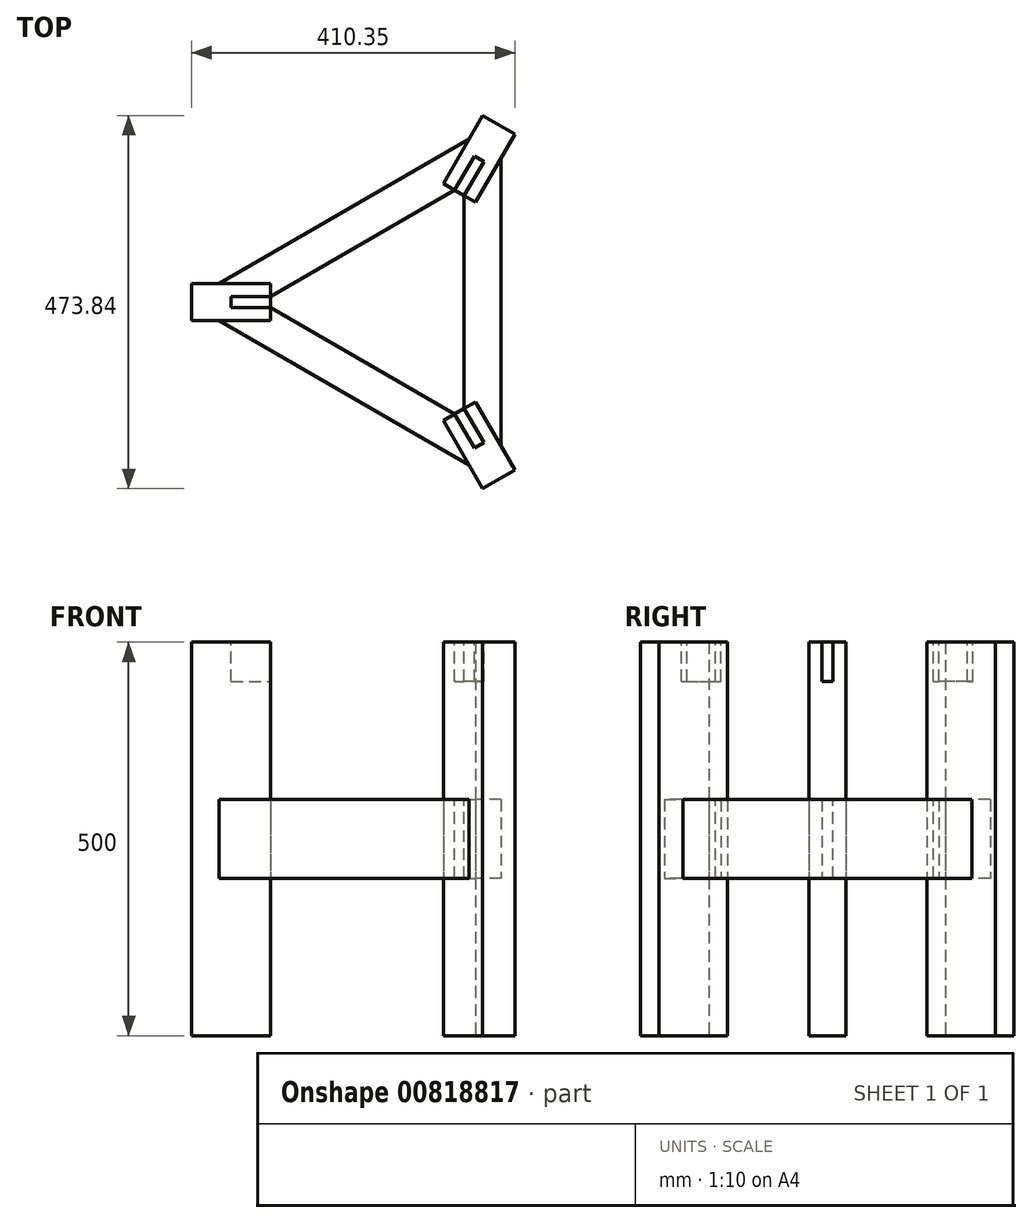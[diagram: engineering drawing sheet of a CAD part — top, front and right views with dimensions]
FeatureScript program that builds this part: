
annotation { "Feature Type Name" : "Feature", "Feature Type Description" : "" }
export const myFeature = defineFeature(function(context is Context, id is Id, definition is map)
    precondition{}
    {
        {
            var Q0;
            Q0=qCreatedBy(makeId("Top.planeOp"),FACE);
            var sketch = newSketch(context, id + "F0", { "sketchPlane" : qUnion([Q0])});
            skLineSegment(sketch, "E0.bottom", {"start": v(-160, 23.5) * mm, "end": v(-260, 23.5) * mm});
            skLineSegment(sketch, "E0.top", {"start": v(-160, -23.5) * mm, "end": v(-260, -23.5) * mm});
            skLineSegment(sketch, "E0.left", {"start": v(-160, 23.5) * mm, "end": v(-160, -23.5) * mm});
            skLineSegment(sketch, "E0.right", {"start": v(-260, 23.5) * mm, "end": v(-260, -23.5) * mm});
            skPoint(sketch, "E0.middle", {"position": v(-210, 0) * mm});
            skSolve(sketch);
        }
        {
            var Q0;
            Q0=makeQuery(id+"F0.imprint","IMPRINT",FACE,{"disambiguationData":[TD([[makeQuery(id+"F0.imprint","IMPRINT",EDGE,{"derivedFrom":sQuery(id+"F0.wireOp",EDGE,"E0.bottom")}),1.0]])]});
            extrude(context, id + "F1", {"entities" : qUnion([Q0]), "depth" : 500 * mm, "offsetDistance" : 25 * mm});
        }
        {
            var Q0;
            Q0=qCreatedBy(makeId("Right.planeOp"),FACE);
            var sketch = newSketch(context, id + "F2", { "sketchPlane" : qUnion([Q0])});
            skLineSegment(sketch, "E1", {"start": v(0, 0) * mm, "end": v(0, 180.45) * mm});
            skSolve(sketch);
        }
        {
            var Q0;
            Q0=makeQuery(id+"F1.opExtrude","CAP_FACE",FACE,{"disambiguationData":[OSD([sQuery(id+"F0.wireOp",EDGE,"E0.bottom"),sQuery(id+"F0.wireOp",EDGE,"E0.top"),sQuery(id+"F0.wireOp",EDGE,"E0.left"),sQuery(id+"F0.wireOp",EDGE,"E0.right")])],"isStart":false});
            var sketch = newSketch(context, id + "F3", { "sketchPlane" : qUnion([Q0])});
            skLineSegment(sketch, "E2.bottom", {"start": v(-210, 7) * mm, "end": v(-160, 7) * mm});
            skLineSegment(sketch, "E2.top", {"start": v(-210, -7) * mm, "end": v(-160, -7) * mm});
            skLineSegment(sketch, "E2.left", {"start": v(-210, 7) * mm, "end": v(-210, -7) * mm});
            skLineSegment(sketch, "E2.right", {"start": v(-160, 7) * mm, "end": v(-160, -7) * mm});
            skPoint(sketch, "E2.middle", {"position": v(-185, 0) * mm});
            skSolve(sketch);
        }
        {
            var Q0;
            Q0 = qSketchRegion(id + "F3", true);
            extrude(context, id + "F4", {"entities" : qUnion([Q0]), "operationType" : NewBodyOperationType.REMOVE, "oppositeDirection" : true, "depth" : 50 * mm, "offsetDistance" : 25 * mm});
        }
        {
            var Q0;
            Q0=makeQuery(id+"F1.opExtrude","SWEPT_BODY",BODY,{"disambiguationData":[OSD([sQuery(id+"F0.wireOp",EDGE,"E0.bottom"),sQuery(id+"F0.wireOp",EDGE,"E0.top"),sQuery(id+"F0.wireOp",EDGE,"E0.left"),sQuery(id+"F0.wireOp",EDGE,"E0.right")])]});
            var Q1;
            Q1=sQuery(id+"F2.wireOp",EDGE,"E1");
            circularPattern(context, id + "F5", {"entities" : qUnion([Q0]), "axis" : qUnion([Q1]), "angle" : 360 * degree, "instanceCount" : 3, "equalSpace" : true});
        }
        {
            var Q0;
            Q0=qCreatedBy(makeId("Top.planeOp"),FACE);
            cPlane(context, id + "F6", {"entities" : qUnion([Q0]), "cplaneType" : CPlaneType.OFFSET, "offset" : 200 * mm, "width" : 150 * mm, "height" : 150 * mm});
        }
        {
            var Q0;
            Q0=qCreatedBy(id+"F6.planeOp",FACE);
            var sketch = newSketch(context, id + "F7", { "sketchPlane" : qUnion([Q0])});
            skLineSegment(sketch, "E3.bottom", {"start": v(92.36, 206.97) * mm, "end": v(-225.42, 23.5) * mm});
            skLineSegment(sketch, "E3.top", {"start": v(115.86, 166.27) * mm, "end": v(-201.92, -17.2) * mm});
            skLineSegment(sketch, "E3.left", {"start": v(92.36, 206.97) * mm, "end": v(115.86, 166.27) * mm});
            skLineSegment(sketch, "E3.right", {"start": v(-225.42, 23.5) * mm, "end": v(-201.92, -17.2) * mm});
            skPoint(sketch, "E3.middle", {"position": v(-54.78, 94.88) * mm});
            skSolve(sketch);
        }
        {
            var Q0;
            Q0=makeQuery(id+"F7.imprint","IMPRINT",FACE,{"disambiguationData":[TD([[makeQuery(id+"F7.imprint","IMPRINT",EDGE,{"derivedFrom":sQuery(id+"F7.wireOp",EDGE,"E3.bottom")}),1.0]])]});
            extrude(context, id + "F8", {"entities" : qUnion([Q0]), "depth" : 100 * mm, "offsetDistance" : 25 * mm});
        }
        {
            var Q0;
            Q0=makeQuery(id+"F1.opExtrude","SWEPT_BODY",BODY,{"disambiguationData":[OSD([sQuery(id+"F0.wireOp",EDGE,"E0.bottom"),sQuery(id+"F0.wireOp",EDGE,"E0.top"),sQuery(id+"F0.wireOp",EDGE,"E0.left"),sQuery(id+"F0.wireOp",EDGE,"E0.right")])]});
            var Q1;
            Q1=makeQuery(id+"F5.opPattern","COPY",BODY,{"derivedFrom":makeQuery(id+"F1.opExtrude","SWEPT_BODY",BODY,{"disambiguationData":[OSD([sQuery(id+"F0.wireOp",EDGE,"E0.bottom"),sQuery(id+"F0.wireOp",EDGE,"E0.top"),sQuery(id+"F0.wireOp",EDGE,"E0.left"),sQuery(id+"F0.wireOp",EDGE,"E0.right")])]}),"instanceName":"2"});
            var Q2;
            Q2=makeQuery(id+"F8.opExtrude","SWEPT_BODY",BODY,{"disambiguationData":[OSD([sQuery(id+"F7.wireOp",EDGE,"E3.bottom"),sQuery(id+"F7.wireOp",EDGE,"E3.top"),sQuery(id+"F7.wireOp",EDGE,"E3.left"),sQuery(id+"F7.wireOp",EDGE,"E3.right")])]});
            booleanBodies(context, id + "F9", {"operationType" : BooleanOperationType.SUBTRACTION, "tools" : qUnion([Q0, Q1]), "targets" : qUnion([Q2]), "keepTools" : true});
        }
        {
            var Q0;
            Q0=makeQuery(id+"F8.opExtrude","SWEPT_BODY",BODY,{"disambiguationData":[OSD([sQuery(id+"F7.wireOp",EDGE,"E3.bottom"),sQuery(id+"F7.wireOp",EDGE,"E3.top"),sQuery(id+"F7.wireOp",EDGE,"E3.left"),sQuery(id+"F7.wireOp",EDGE,"E3.right")])]});
            var Q1;
            Q1=sQuery(id+"F2.wireOp",EDGE,"E1");
            circularPattern(context, id + "F10", {"entities" : qUnion([Q0]), "axis" : qUnion([Q1]), "angle" : 360 * degree, "instanceCount" : 3, "equalSpace" : true});
        }
    });
